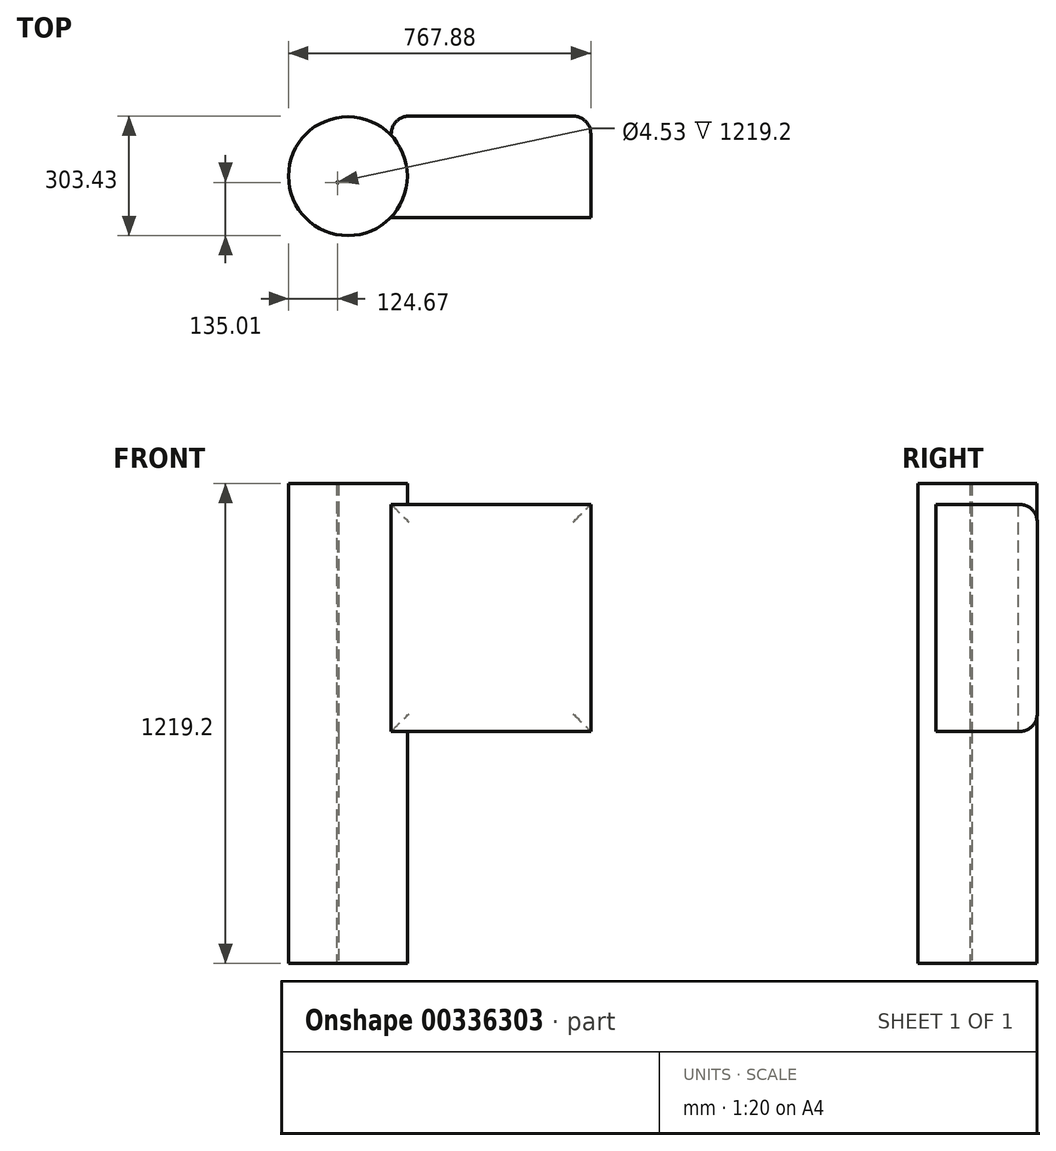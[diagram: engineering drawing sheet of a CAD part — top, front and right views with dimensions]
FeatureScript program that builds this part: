
annotation { "Feature Type Name" : "Feature", "Feature Type Description" : "" }
export const myFeature = defineFeature(function(context is Context, id is Id, definition is map)
    precondition{}
    {
        {
            var Q0;
            Q0=qCreatedBy(makeId("Top.planeOp"),FACE);
            var sketch = newSketch(context, id + "F0", { "sketchPlane" : qUnion([Q0])});
            skCircle(sketch, "E0", {"center": v(0, 0) * mm, "radius": 2.26 * mm});
            skCircle(sketch, "E1", {"center": v(26.32, 15.98) * mm, "radius": 150.99 * mm});
            skSolve(sketch);
        }
        {
            var Q0;
            Q0=makeQuery(id+"F0.imprint","IMPRINT",FACE,{"disambiguationData":[TD([[makeQuery(id+"F0.imprint","IMPRINT",EDGE,{"derivedFrom":sQuery(id+"F0.wireOp",EDGE,"E0")}),-1.0]])]});
            extrude(context, id + "F1", {"entities" : qUnion([Q0]), "depth" : 1219.2 * mm});
        }
        {
            var Q0;
            Q0=qCreatedBy(makeId("Right.planeOp"),FACE);
            var sketch = newSketch(context, id + "F2", { "sketchPlane" : qUnion([Q0])});
            skLineSegment(sketch, "E2.bottom", {"start": v(0, 645.4) * mm, "end": v(0, 645.4) * mm});
            skLineSegment(sketch, "E2.top", {"start": v(0, 650.73) * mm, "end": v(0, 650.73) * mm});
            skLineSegment(sketch, "E2.left", {"start": v(0, 645.4) * mm, "end": v(0, 650.73) * mm});
            skLineSegment(sketch, "E2.right", {"start": v(0, 645.4) * mm, "end": v(0, 650.73) * mm});
            skLineSegment(sketch, "E3.bottom", {"start": v(119.42, 589.35) * mm, "end": v(0, 589.35) * mm});
            skLineSegment(sketch, "E3.top", {"start": v(119.42, 645.4) * mm, "end": v(0, 645.4) * mm});
            skLineSegment(sketch, "E3.left", {"start": v(119.42, 589.35) * mm, "end": v(119.42, 645.4) * mm});
            skLineSegment(sketch, "E3.right", {"start": v(0, 589.35) * mm, "end": v(0, 645.4) * mm});
            skSolve(sketch);
        }
        {
            var Q0;
            Q0=sQuery(id+"F2.wireOp",EDGE,"E3.bottom");
            extrude(context, id + "F3", {"bodyType" : ToolBodyType.SURFACE, "surfaceEntities" : qUnion([Q0]), "depth" : 643.2 * mm});
        }
        {
            var Q0;
            Q0=makeQuery(id+"F3.opExtrude","SWEPT_FACE",FACE,{"disambiguationData":[OSD([sQuery(id+"F2.wireOp",EDGE,"E3.bottom")])]});
            extrude(context, id + "F4", {"entities" : qUnion([Q0]), "operationType" : NewBodyOperationType.ADD, "depth" : 576.66 * mm});
        }
        {
            var Q0;
            Q0=makeQuery(id+"F4.opExtrude","SWEPT_FACE",FACE,{"disambiguationData":[OSD([sQuery(id+"F2.wireOp",VERTEX,"E3.bottom.start")])]});
            extrude(context, id + "F5", {"entities" : qUnion([Q0]), "operationType" : NewBodyOperationType.ADD, "depth" : 49 * mm});
        }
        {
            var Q0;
            Q0=makeQuery(id+"F5.opExtrude","CAP_FACE",FACE,{"disambiguationData":[OSD([sQuery(id+"F2.wireOp",VERTEX,"E3.bottom.start")])],"isStart":false});
            var sketch = newSketch(context, id + "F6", { "sketchPlane" : qUnion([Q0])});
            skLineSegment(sketch, "E4", {"start": v(-136.3, 1166) * mm, "end": v(-643.2, 1166) * mm});
            skSolve(sketch);
        }
        {
            var Q0;
            Q0=makeQuery(id+"F6.imprint","IMPRINT",FACE,{"disambiguationData":[TD([[makeQuery(id+"F6.imprint","IMPRINT",EDGE,{"derivedFrom":sQuery(id+"F6.wireOp",EDGE,"E4")}),1.0]])]});
            var sketch = newSketch(context, id + "F7", { "sketchPlane" : qUnion([Q0])});
            skSolve(sketch);
        }
        {
            var Q0;
            Q0=makeQuery(id+"F6.imprint","IMPRINT",FACE,{"disambiguationData":[TD([[makeQuery(id+"F6.imprint","IMPRINT",EDGE,{"derivedFrom":sQuery(id+"F6.wireOp",EDGE,"E4")}),1.0]])]});
            extrude(context, id + "F8", {"entities" : qUnion([Q0]), "operationType" : NewBodyOperationType.ADD, "oppositeDirection" : true, "depth" : 258.02 * mm});
        }
        {
            var Q0;
            Q0=makeQuery(id+"F5.opExtrude","CAP_FACE",FACE,{"disambiguationData":[OSD([sQuery(id+"F2.wireOp",VERTEX,"E3.bottom.start")])],"isStart":false});
            fillet(context, id + "F9", {"entities" : qUnion([Q0]), "radius" : 44.72 * mm, "tangentPropagation" : true, "allowEdgeOverflow" : false});
        }
    });
